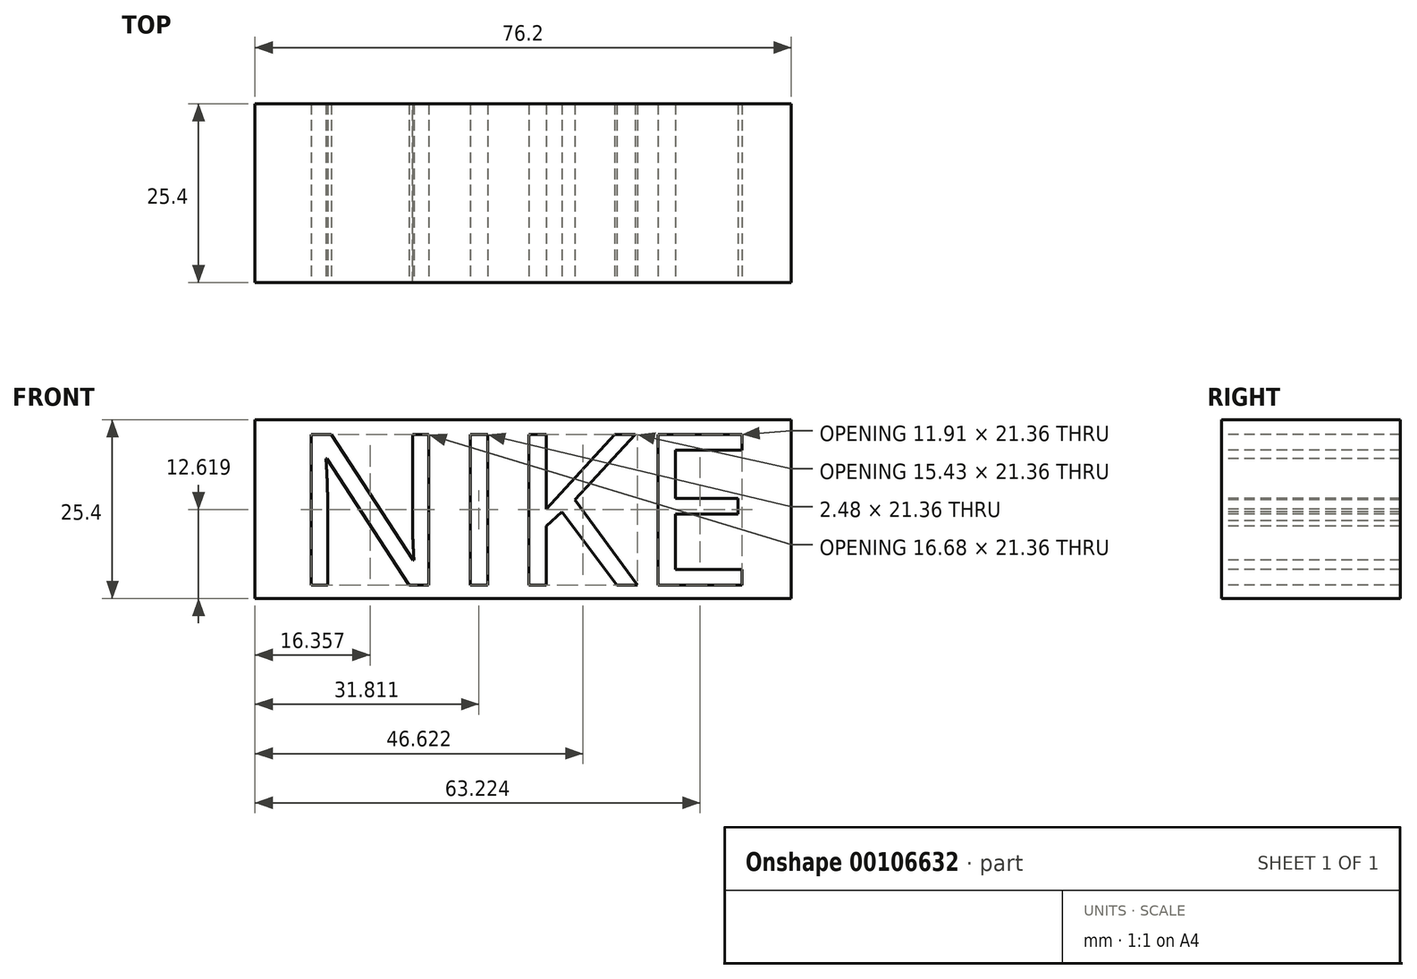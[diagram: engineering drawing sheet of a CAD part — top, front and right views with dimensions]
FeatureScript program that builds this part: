
annotation { "Feature Type Name" : "Feature", "Feature Type Description" : "" }
export const myFeature = defineFeature(function(context is Context, id is Id, definition is map)
    precondition{}
    {
        {
            var Q0;
            Q0=qCreatedBy(makeId("Front.planeOp"),FACE);
            var sketch = newSketch(context, id + "F0", { "sketchPlane" : qUnion([Q0])});
            skLineSegment(sketch, "E0", {"start": v(0, 0) * mm, "end": v(0, 50.8) * mm});
            skLineSegment(sketch, "E1", {"start": v(0, 50.8) * mm, "end": v(76.2, 50.8) * mm});
            skLineSegment(sketch, "E2", {"start": v(76.2, 50.8) * mm, "end": v(76.2, 0) * mm});
            skLineSegment(sketch, "E3", {"start": v(76.2, 0) * mm, "end": v(0, 0) * mm});
            skSolve(sketch);
        }
        {
            var Q0;
            Q0 = qSketchRegion(id + "F0", true);
            extrude(context, id + "F1", {"entities" : qUnion([Q0]), "depth" : 25.4 * mm});
        }
        {
            var Q0;
            Q0=makeQuery(id+"F1.opExtrude","CAP_FACE",FACE,{"disambiguationData":[OSD([sQuery(id+"F0.wireOp",EDGE,"E0"),sQuery(id+"F0.wireOp",EDGE,"E1"),sQuery(id+"F0.wireOp",EDGE,"E2"),sQuery(id+"F0.wireOp",EDGE,"E3")])],"isStart":false});
            var sketch = newSketch(context, id + "F2", { "sketchPlane" : qUnion([Q0])});
            skText(sketch, "E4", { "text": "NIKE", "fontName": "OpenSans-Regular.ttf"});
            const initialGuessF2  = {"E4": [0.00508, 0.00194, 1, 0, 0.02154]};
            skSetInitialGuess(sketch, initialGuessF2);
            skSolve(sketch);
        }
        {
            var Q0;
            Q0 = qSketchRegion(id + "F2", true);
            extrude(context, id + "F3", {"entities" : qUnion([Q0]), "operationType" : NewBodyOperationType.REMOVE, "oppositeDirection" : true, "depth" : 25.4 * mm});
        }
        {
            var Q0;
            Q0=makeQuery(id+"F1.opExtrude","CAP_FACE",FACE,{"disambiguationData":[OSD([sQuery(id+"F0.wireOp",EDGE,"E0"),sQuery(id+"F0.wireOp",EDGE,"E1"),sQuery(id+"F0.wireOp",EDGE,"E2"),sQuery(id+"F0.wireOp",EDGE,"E3")])],"isStart":false});
            var sketch = newSketch(context, id + "F4", { "sketchPlane" : qUnion([Q0])});
            skLineSegment(sketch, "E5", {"start": v(0, 25.4) * mm, "end": v(76.2, 25.4) * mm});
            skSolve(sketch);
        }
        {
            var Q0;
            {var subQ0=sQuery(id+"F4.wireOp",EDGE,"E5");Q0=makeQuery(id+"F4.imprint","IMPRINT",FACE,{"disambiguationData":[TD([[makeQuery(id+"F4.imprint","IMPRINT",EDGE,{"derivedFrom":subQ0}),1.0]])]});}
            extrude(context, id + "F5", {"entities" : qUnion([Q0]), "operationType" : NewBodyOperationType.REMOVE, "oppositeDirection" : true, "depth" : 25.4 * mm});
        }
    });
